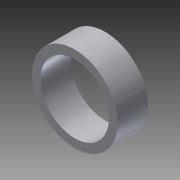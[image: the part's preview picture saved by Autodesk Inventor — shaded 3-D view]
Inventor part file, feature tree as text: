
AUTODESK INVENTOR PART (.ipt)
format: ipt  version: 2014 SP1 (Build 180222100, 222)  size: 96,768 bytes
history: native  units: in
note: dims shown in document units (in); Inventor stores cm internally (conversion verified against a paired STEP export)
features: extrude x1, sketch x1
ambient origin geometry x8: Origin, YZ Plane, XZ Plane, XY Plane, X Axis, Y Axis, Z Axis, Center Point
bodies: Solid1 (feature_tree)
feature tree (2):
  extrude  "Extrusion1"  Depth=0.223in
  sketch  "Sketch1"  dims[d0=0.5in d1=0.625in d2=0.223in d3=0.0in]
